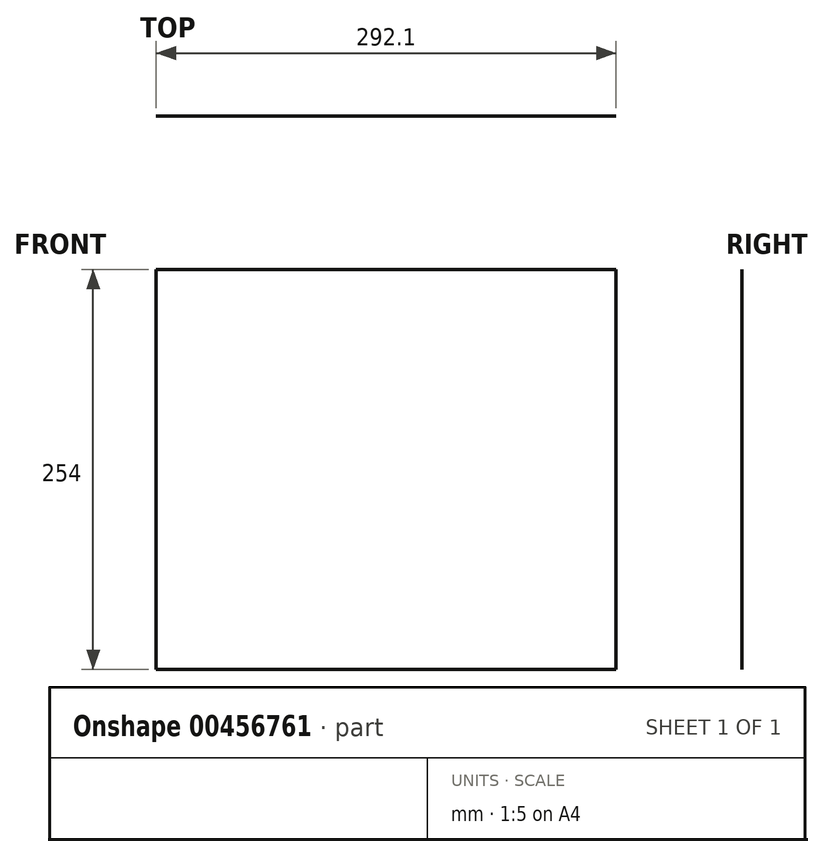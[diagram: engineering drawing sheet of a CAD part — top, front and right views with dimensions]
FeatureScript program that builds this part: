
annotation { "Feature Type Name" : "Feature", "Feature Type Description" : "" }
export const myFeature = defineFeature(function(context is Context, id is Id, definition is map)
    precondition{}
    {
        {
            var Q0;
            Q0=qCreatedBy(makeId("Front.planeOp"),FACE);
            var sketch = newSketch(context, id + "F0", { "sketchPlane" : qUnion([Q0])});
            skLineSegment(sketch, "E0.bottom", {"start": v(-146.05, 127) * mm, "end": v(146.05, 127) * mm});
            skLineSegment(sketch, "E0.top", {"start": v(-146.05, -127) * mm, "end": v(146.05, -127) * mm});
            skLineSegment(sketch, "E0.left", {"start": v(-146.05, 127) * mm, "end": v(-146.05, -127) * mm});
            skLineSegment(sketch, "E0.right", {"start": v(146.05, 127) * mm, "end": v(146.05, -127) * mm});
            skPoint(sketch, "E0.middle", {"position": v(0, 0) * mm});
            skSolve(sketch);
        }
        {
            var Q0;
            Q0=makeQuery(id+"F0.imprint","IMPRINT",FACE,{"disambiguationData":[TD([[makeQuery(id+"F0.imprint","IMPRINT",EDGE,{"derivedFrom":sQuery(id+"F0.wireOp",EDGE,"E0.bottom")}),-1.0]])]});
            extrude(context, id + "F1", {"entities" : qUnion([Q0]), "depth" : 1 / 203.2 * mm});
        }
    });
